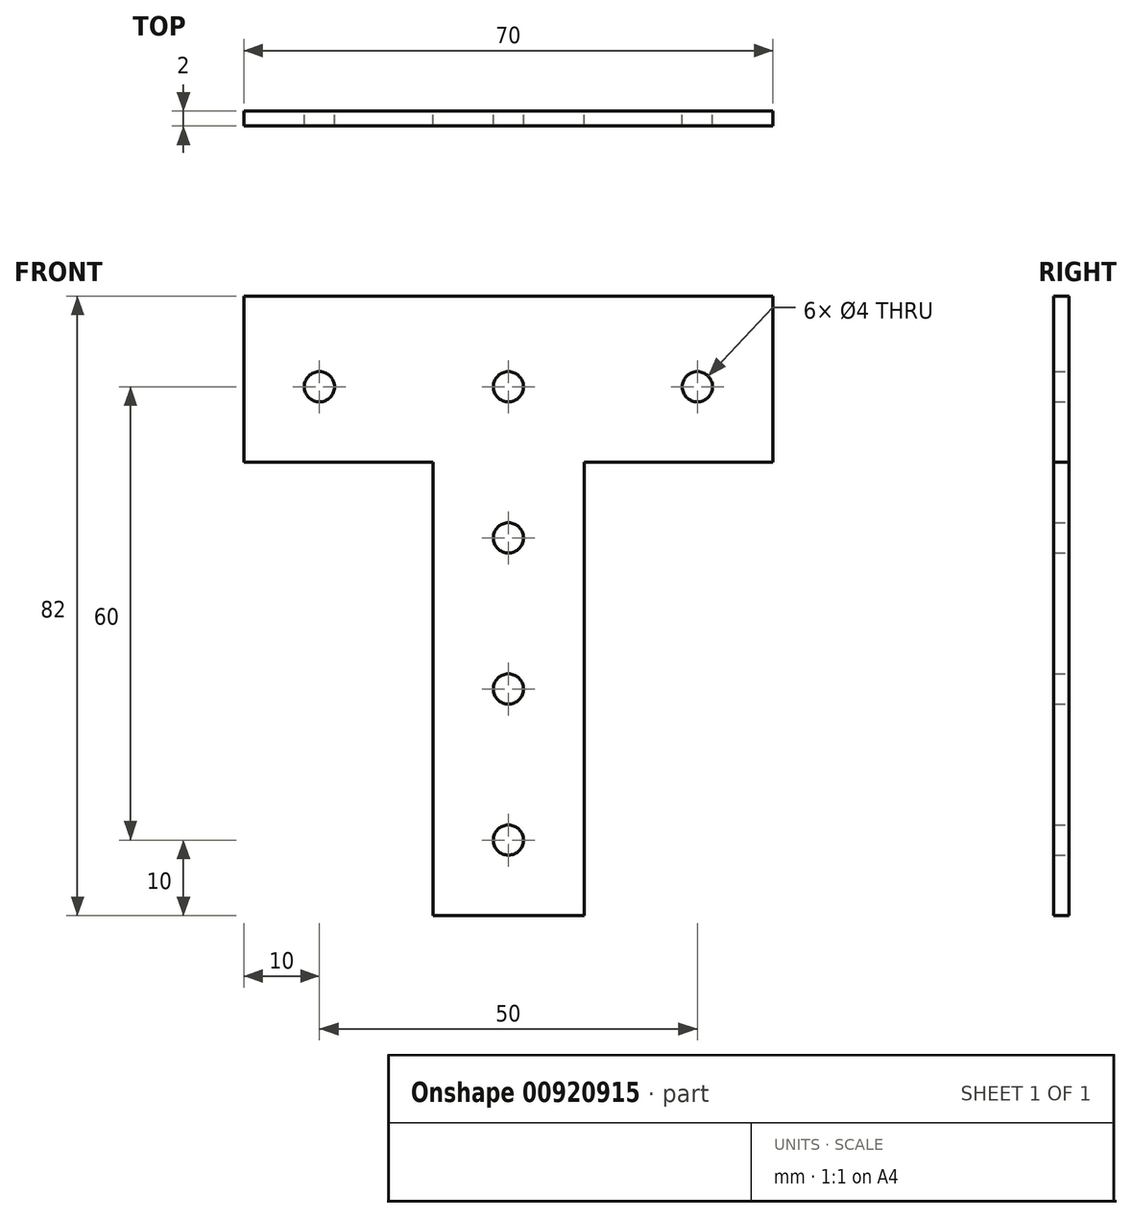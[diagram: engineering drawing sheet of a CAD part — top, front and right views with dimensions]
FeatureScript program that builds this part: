
annotation { "Feature Type Name" : "Feature", "Feature Type Description" : "" }
export const myFeature = defineFeature(function(context is Context, id is Id, definition is map)
    precondition{}
    {
        {
            var Q0;
            Q0=qCreatedBy(makeId("Front.planeOp"),FACE);
            var sketch = newSketch(context, id + "F0", { "sketchPlane" : qUnion([Q0])});
            skLineSegment(sketch, "E0.bottom", {"start": v(0, 0) * mm, "end": v(70, 0) * mm});
            skLineSegment(sketch, "E0.top", {"start": v(0, -22) * mm, "end": v(25, -22) * mm});
            skLineSegment(sketch, "E0.left", {"start": v(0, 0) * mm, "end": v(0, -22) * mm});
            skLineSegment(sketch, "E0.right", {"start": v(70, 0) * mm, "end": v(70, -22) * mm});
            skLineSegment(sketch, "E1", {"start": v(25, -22) * mm, "end": v(25, -82) * mm});
            skLineSegment(sketch, "E2", {"start": v(25, -82) * mm, "end": v(45, -82) * mm});
            skLineSegment(sketch, "E3", {"start": v(45, -82) * mm, "end": v(45, -22) * mm});
            skLineSegment(sketch, "E4.trimOffspring", {"start": v(45, -22) * mm, "end": v(70, -22) * mm});
            skCircle(sketch, "E5", {"center": v(10, -12) * mm, "radius": 2 * mm});
            skCircle(sketch, "E6", {"center": v(35, -12) * mm, "radius": 2 * mm});
            skPoint(sketch, "E6.centerSnap0", {"position": v(35, -82) * mm});
            skCircle(sketch, "E7", {"center": v(60, -12) * mm, "radius": 2 * mm});
            skCircle(sketch, "E8", {"center": v(35, -32) * mm, "radius": 2 * mm});
            skCircle(sketch, "E9", {"center": v(35, -52) * mm, "radius": 2 * mm});
            skCircle(sketch, "E10", {"center": v(35, -72) * mm, "radius": 2 * mm});
            skSolve(sketch);
        }
        {
            var Q0;
            Q0 = qSketchRegion(id + "F0", true);
            extrude(context, id + "F1", {"entities" : qUnion([Q0]), "depth" : 2 * mm, "offsetDistance" : 25 * mm});
        }
    });
